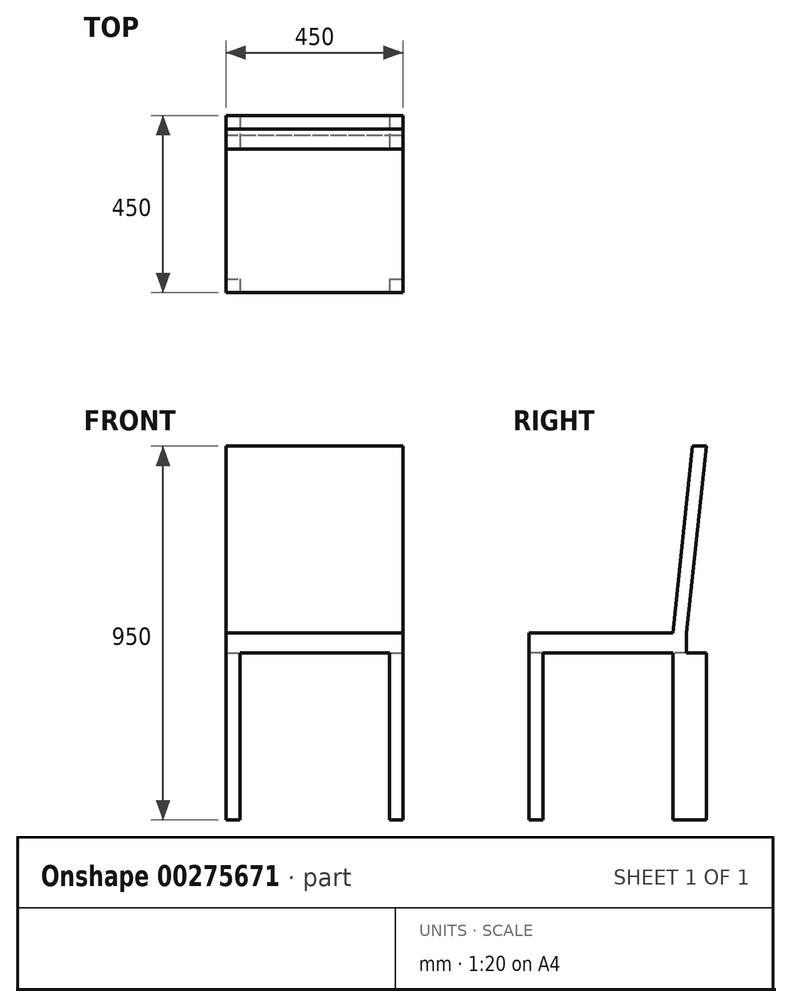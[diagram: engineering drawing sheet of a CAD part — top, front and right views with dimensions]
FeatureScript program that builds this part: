
annotation { "Feature Type Name" : "Feature", "Feature Type Description" : "" }
export const myFeature = defineFeature(function(context is Context, id is Id, definition is map)
    precondition{}
    {
        {
            var Q0;
            Q0=qCreatedBy(makeId("Top.planeOp"),FACE);
            var sketch = newSketch(context, id + "F0", { "sketchPlane" : qUnion([Q0])});
            skLineSegment(sketch, "E0.bottom", {"start": v(225, 225) * mm, "end": v(-225, 225) * mm});
            skLineSegment(sketch, "E0.top", {"start": v(225, -225) * mm, "end": v(-225, -225) * mm});
            skLineSegment(sketch, "E0.left", {"start": v(225, 225) * mm, "end": v(225, -225) * mm});
            skLineSegment(sketch, "E0.right", {"start": v(-225, 225) * mm, "end": v(-225, -225) * mm});
            skPoint(sketch, "E0.middle", {"position": v(0, 0) * mm});
            skSolve(sketch);
        }
        {
            var Q0;
            Q0=qSketchRegion(id+"F0",true);
            extrude(context, id + "F1", {"entities" : qUnion([Q0]), "depth" : 950 * mm});
        }
        {
            var Q0;
            Q0=makeQuery(id+"F1.opExtrude","SWEPT_FACE",FACE,{"disambiguationData":[OSD([sQuery(id+"F0.wireOp",EDGE,"E0.left")])]});
            var sketch = newSketch(context, id + "F2", { "sketchPlane" : qUnion([Q0])});
            skLineSegment(sketch, "E1.bottom", {"start": v(-225, 475) * mm, "end": v(225, 475) * mm});
            skLineSegment(sketch, "E1.top", {"start": v(-225, 425) * mm, "end": v(225, 425) * mm});
            skLineSegment(sketch, "E1.left", {"start": v(-225, 475) * mm, "end": v(-225, 425) * mm});
            skLineSegment(sketch, "E1.right", {"start": v(225, 475) * mm, "end": v(225, 425) * mm});
            skLineSegment(sketch, "E2", {"start": v(225, 425) * mm, "end": v(175, 425) * mm});
            skLineSegment(sketch, "E3", {"start": v(175, 475) * mm, "end": v(225, 950) * mm});
            skLineSegment(sketch, "E4", {"start": v(190, 950) * mm, "end": v(140, 475) * mm});
            skLineSegment(sketch, "E5", {"start": v(140, 475) * mm, "end": v(140, 0) * mm});
            skLineSegment(sketch, "E6", {"start": v(175, 425) * mm, "end": v(175, 0) * mm});
            skLineSegment(sketch, "E7", {"start": v(-225, 425) * mm, "end": v(-190, 425) * mm});
            skLineSegment(sketch, "E8", {"start": v(-190, 425) * mm, "end": v(-190, 0) * mm});
            skLineSegment(sketch, "E9", {"start": v(175, 475) * mm, "end": v(175, 425) * mm});
            skSolve(sketch);
        }
        {
            var Q0;
            {var subQ4=sQuery(id+"F2.wireOp",EDGE,"E4");Q0=makeQuery(id+"F2.imprint","IMPRINT",FACE,{"disambiguationData":[TD([[makeQuery(id+"F2.imprint","IMPRINT",EDGE,{"derivedFrom":subQ4}),-1.0]])]});}
            var Q1;
            {var subQ0=sQuery(id+"F2.wireOp",EDGE,"E8");Q1=makeQuery(id+"F2.imprint","IMPRINT",FACE,{"disambiguationData":[TD([[makeQuery(id+"F2.imprint","IMPRINT",EDGE,{"derivedFrom":subQ0}),1.0]])]});}
            var Q2;
            {var subQ0=sQuery(id+"F2.wireOp",EDGE,"E2");Q2=makeQuery(id+"F2.imprint","IMPRINT",FACE,{"disambiguationData":[TD([[makeQuery(id+"F2.imprint","IMPRINT",EDGE,{"derivedFrom":subQ0}),1.0]])]});}
            var Q3;
            {var subQ4=sQuery(id+"F2.wireOp",EDGE,"E3");Q3=makeQuery(id+"F2.imprint","IMPRINT",FACE,{"disambiguationData":[TD([[makeQuery(id+"F2.imprint","IMPRINT",EDGE,{"derivedFrom":subQ4}),-1.0]])]});}
            var Q4;
            {var subQ0=sQuery(id+"F2.wireOp",EDGE,"E1.right");Q4=makeQuery(id+"F2.imprint","IMPRINT",FACE,{"disambiguationData":[TD([[makeQuery(id+"F2.imprint","IMPRINT",EDGE,{"derivedFrom":subQ0}),-1.0]])]});}
            extrude(context, id + "F3", {"entities" : qUnion([Q0, Q1, Q2, Q3, Q4]), "operationType" : NewBodyOperationType.REMOVE, "endBound" : BoundingType.THROUGH_ALL, "oppositeDirection" : true, "depth" : 25 * mm});
        }
        {
            var Q0;
            Q0=makeQuery(id+"F1.opExtrude","SWEPT_FACE",FACE,{"disambiguationData":[OSD([sQuery(id+"F0.wireOp",EDGE,"E0.top")])]});
            var sketch = newSketch(context, id + "F4", { "sketchPlane" : qUnion([Q0])});
            skLineSegment(sketch, "E10", {"start": v(-225, 0) * mm, "end": v(-190, 0) * mm});
            skLineSegment(sketch, "E11", {"start": v(-190, 0) * mm, "end": v(225, 0) * mm});
            skLineSegment(sketch, "E12", {"start": v(225, 0) * mm, "end": v(190, 0) * mm});
            skLineSegment(sketch, "E13", {"start": v(-190, 0) * mm, "end": v(-190, 425) * mm});
            skLineSegment(sketch, "E14", {"start": v(190, 0) * mm, "end": v(190, 425) * mm});
            skLineSegment(sketch, "E15", {"start": v(190, 425) * mm, "end": v(-190, 425) * mm});
            skSolve(sketch);
        }
        {
            var Q0;
            Q0=makeQuery(id+"F4.imprint","IMPRINT",FACE,{"disambiguationData":[TD([[makeQuery(id+"F4.imprint","IMPRINT",EDGE,{"derivedFrom":sQuery(id+"F4.wireOp",EDGE,"E11")}),-1.0]])]});
            extrude(context, id + "F5", {"entities" : qUnion([Q0]), "operationType" : NewBodyOperationType.REMOVE, "endBound" : BoundingType.THROUGH_ALL, "oppositeDirection" : true, "depth" : 25 * mm});
        }
    });
